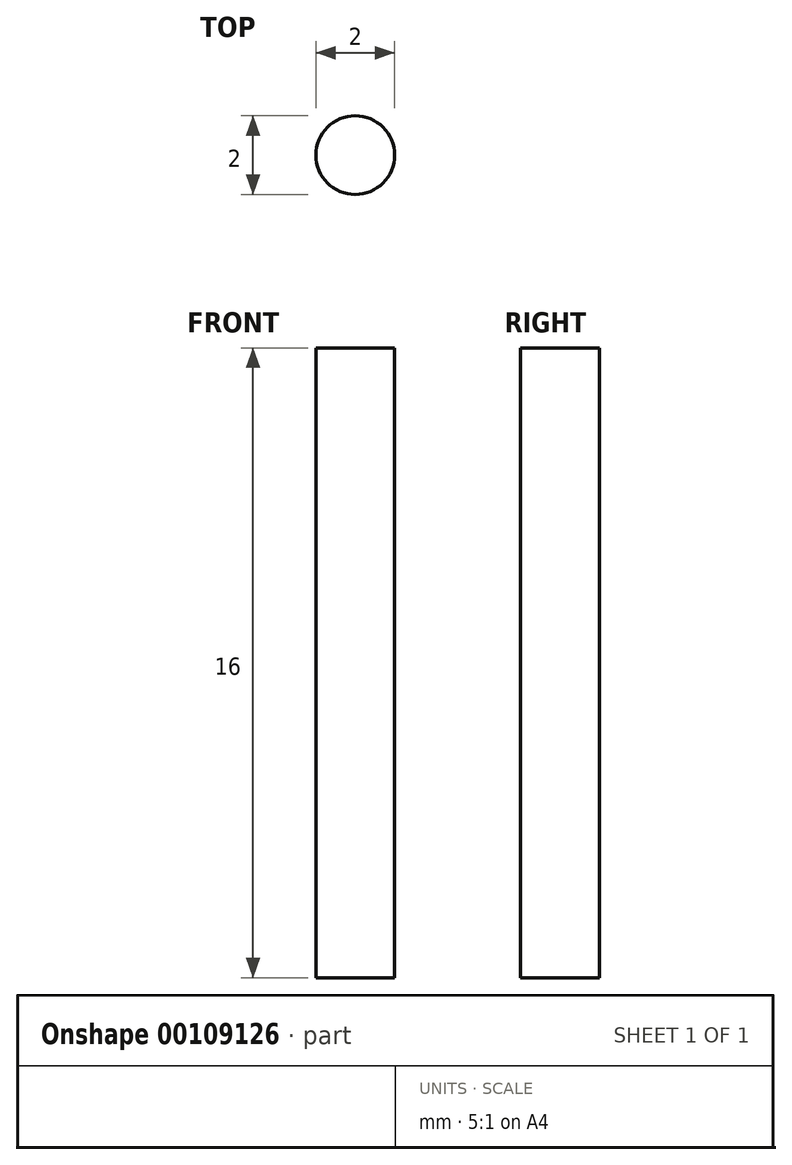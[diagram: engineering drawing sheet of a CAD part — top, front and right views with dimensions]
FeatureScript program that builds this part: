
annotation { "Feature Type Name" : "Feature", "Feature Type Description" : "" }
export const myFeature = defineFeature(function(context is Context, id is Id, definition is map)
    precondition{}
    {
        {
            var Q0;
            Q0=qCreatedBy(makeId("Top.planeOp"),FACE);
            var sketch = newSketch(context, id + "F0", { "sketchPlane" : qUnion([Q0])});
            skCircle(sketch, "E0", {"center": v(0, 0) * mm, "radius": 1 * mm});
            skSolve(sketch);
        }
        {
            var Q0;
            Q0 = qSketchRegion(id + "F0", true);
            var Q1;
            Q1=makeQuery(id+"F0.imprint","IMPRINT",FACE,{"disambiguationData":[TD([[makeQuery(id+"F0.imprint","IMPRINT",EDGE,{"derivedFrom":sQuery(id+"F0.wireOp",EDGE,"E0")}),1.0]])]});
            extrude(context, id + "F1", {"entities" : qUnion([Q0, Q1]), "depth" : 16 * mm});
        }
    });
